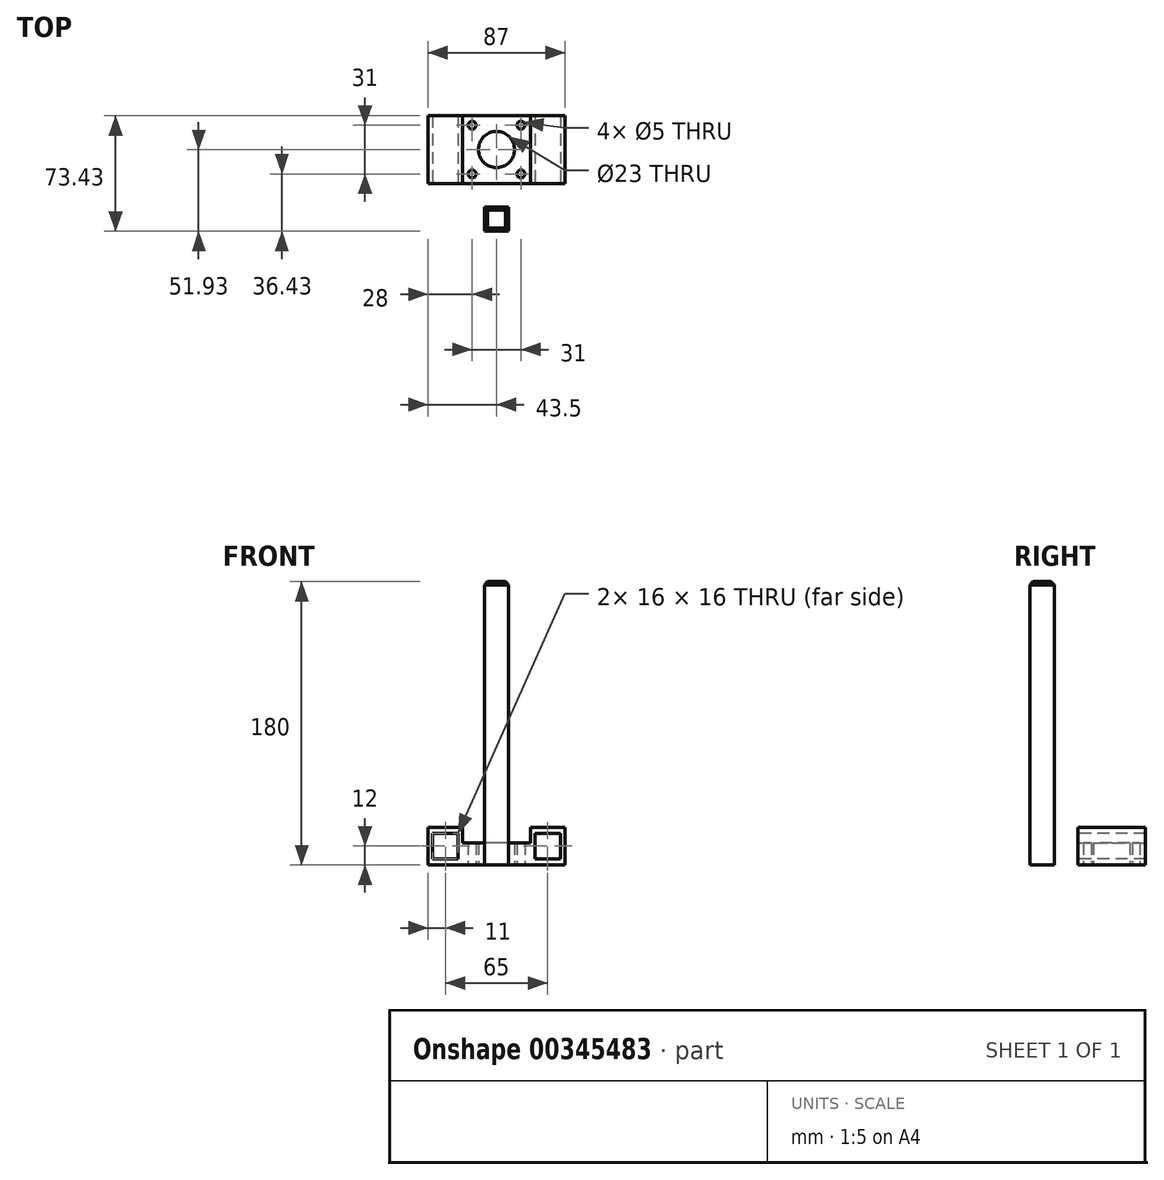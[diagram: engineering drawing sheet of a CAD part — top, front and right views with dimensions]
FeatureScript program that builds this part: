
annotation { "Feature Type Name" : "Feature", "Feature Type Description" : "" }
export const myFeature = defineFeature(function(context is Context, id is Id, definition is map)
    precondition{}
    {
        {
            var Q0;
            Q0=qCreatedBy(makeId("Top.planeOp"),FACE);
            var sketch = newSketch(context, id + "F0", { "sketchPlane" : qUnion([Q0])});
            skPoint(sketch, "E0", {"position": v(0, 0) * mm});
            skLineSegment(sketch, "E1.bottom", {"start": v(15.5, -15.5) * mm, "end": v(-15.5, -15.5) * mm, "construction": true});
            skLineSegment(sketch, "E1.top", {"start": v(15.5, 15.5) * mm, "end": v(-15.5, 15.5) * mm, "construction": true});
            skLineSegment(sketch, "E1.left", {"start": v(15.5, -15.5) * mm, "end": v(15.5, 15.5) * mm, "construction": true});
            skLineSegment(sketch, "E1.right", {"start": v(-15.5, -15.5) * mm, "end": v(-15.5, 15.5) * mm, "construction": true});
            skCircle(sketch, "E2", {"center": v(15.5, 15.5) * mm, "radius": 2.5 * mm});
            skCircle(sketch, "E3", {"center": v(15.5, -15.5) * mm, "radius": 2.5 * mm});
            skCircle(sketch, "E4", {"center": v(-15.5, -15.5) * mm, "radius": 2.5 * mm});
            skCircle(sketch, "E5", {"center": v(-15.5, 15.5) * mm, "radius": 2.5 * mm});
            skCircle(sketch, "E6", {"center": v(0, 0) * mm, "radius": 11.5 * mm});
            skLineSegment(sketch, "E7.bottom", {"start": v(21.5, -21.5) * mm, "end": v(-21.5, -21.5) * mm});
            skLineSegment(sketch, "E7.top", {"start": v(21.5, 21.5) * mm, "end": v(-21.5, 21.5) * mm});
            skLineSegment(sketch, "E7.left", {"start": v(21.5, -21.5) * mm, "end": v(21.5, 21.5) * mm});
            skLineSegment(sketch, "E7.right", {"start": v(-21.5, -21.5) * mm, "end": v(-21.5, 21.5) * mm});
            skLineSegment(sketch, "E8.bottom", {"start": v(-21.5, 21.5) * mm, "end": v(-43.5, 21.5) * mm});
            skLineSegment(sketch, "E8.top", {"start": v(-21.5, -21.5) * mm, "end": v(-43.5, -21.5) * mm});
            skLineSegment(sketch, "E8.left", {"start": v(-21.5, 21.5) * mm, "end": v(-21.5, -21.5) * mm});
            skLineSegment(sketch, "E8.right", {"start": v(-43.5, 21.5) * mm, "end": v(-43.5, -21.5) * mm});
            skLineSegment(sketch, "E9.MirrorCS", {"start": v(21.5, 21.5) * mm, "end": v(43.5, 21.5) * mm});
            skLineSegment(sketch, "E10.MirrorCS", {"start": v(43.5, 21.5) * mm, "end": v(43.5, -21.5) * mm});
            skLineSegment(sketch, "E11.MirrorCS", {"start": v(21.5, -21.5) * mm, "end": v(43.5, -21.5) * mm});
            skLineSegment(sketch, "E12.bottom", {"start": v(7.7, -51.93) * mm, "end": v(-7.7, -51.93) * mm});
            skLineSegment(sketch, "E12.top", {"start": v(7.7, -36.53) * mm, "end": v(-7.7, -36.53) * mm});
            skLineSegment(sketch, "E12.left", {"start": v(7.7, -51.93) * mm, "end": v(7.7, -36.53) * mm});
            skLineSegment(sketch, "E12.right", {"start": v(-7.7, -51.93) * mm, "end": v(-7.7, -36.53) * mm});
            skPoint(sketch, "E12.middle", {"position": v(0, -44.23) * mm});
            skSolve(sketch);
        }
        {
            var Q0;
            Q0=makeQuery(id+"F0.imprint","IMPRINT",FACE,{"disambiguationData":[TD([[makeQuery(id+"F0.imprint","IMPRINT",EDGE,{"derivedFrom":sQuery(id+"F0.wireOp",EDGE,"E2")}),-1.0]])]});
            extrude(context, id + "F1", {"entities" : qUnion([Q0]), "depth" : 14 * mm});
        }
        {
            var Q0;
            Q0=makeQuery(id+"F0.imprint","IMPRINT",FACE,{"disambiguationData":[TD([[makeQuery(id+"F0.imprint","IMPRINT",EDGE,{"derivedFrom":sQuery(id+"F0.wireOp",EDGE,"E8.bottom")}),1.0]])]});
            var Q1;
            Q1=makeQuery(id+"F0.imprint","IMPRINT",FACE,{"disambiguationData":[TD([[makeQuery(id+"F0.imprint","IMPRINT",EDGE,{"derivedFrom":sQuery(id+"F0.wireOp",EDGE,"E7.left")}),-1.0]])]});
            extrude(context, id + "F2", {"entities" : qUnion([Q0, Q1]), "operationType" : NewBodyOperationType.ADD, "depth" : 24 * mm});
        }
        {
            var Q0;
            Q0=makeQuery(id+"F2.opExtrude","SWEPT_FACE",FACE,{"disambiguationData":[OSD([sQuery(id+"F0.wireOp",EDGE,"E8.top")])]});
            var sketch = newSketch(context, id + "F3", { "sketchPlane" : qUnion([Q0])});
            skLineSegment(sketch, "E13.bottom", {"start": v(-24.5, 4) * mm, "end": v(-40.5, 4) * mm});
            skLineSegment(sketch, "E13.top", {"start": v(-24.5, 20) * mm, "end": v(-40.5, 20) * mm});
            skLineSegment(sketch, "E13.left", {"start": v(-24.5, 4) * mm, "end": v(-24.5, 20) * mm});
            skLineSegment(sketch, "E13.right", {"start": v(-40.5, 4) * mm, "end": v(-40.5, 20) * mm});
            skPoint(sketch, "E13.middle", {"position": v(-32.5, 12) * mm});
            skLineSegment(sketch, "E14.MirrorCS", {"start": v(24.5, 4) * mm, "end": v(40.5, 4) * mm});
            skLineSegment(sketch, "E15.MirrorCS", {"start": v(24.5, 4) * mm, "end": v(24.5, 20) * mm});
            skPoint(sketch, "E16.MirrorP", {"position": v(32.5, 12) * mm});
            skLineSegment(sketch, "E17.MirrorCS", {"start": v(40.5, 4) * mm, "end": v(40.5, 20) * mm});
            skLineSegment(sketch, "E18.MirrorCS", {"start": v(24.5, 20) * mm, "end": v(40.5, 20) * mm});
            skSolve(sketch);
        }
        {
            var Q0;
            Q0=makeQuery(id+"F3.imprint","IMPRINT",FACE,{"disambiguationData":[TD([[makeQuery(id+"F3.imprint","IMPRINT",EDGE,{"derivedFrom":sQuery(id+"F3.wireOp",EDGE,"E13.bottom")}),-1.0]])]});
            var Q1;
            Q1=makeQuery(id+"F3.imprint","IMPRINT",FACE,{"disambiguationData":[TD([[makeQuery(id+"F3.imprint","IMPRINT",EDGE,{"derivedFrom":sQuery(id+"F3.wireOp",EDGE,"E14.MirrorCS")}),1.0]])]});
            extrude(context, id + "F4", {"entities" : qUnion([Q0, Q1]), "operationType" : NewBodyOperationType.REMOVE, "endBound" : BoundingType.UP_TO_NEXT, "oppositeDirection" : true, "depth" : 25 * mm});
        }
        {
            var Q0;
            Q0=makeQuery(id+"F0.imprint","IMPRINT",FACE,{"disambiguationData":[TD([[makeQuery(id+"F0.imprint","IMPRINT",EDGE,{"derivedFrom":sQuery(id+"F0.wireOp",EDGE,"E12.bottom")}),-1.0]])]});
            extrude(context, id + "F5", {"entities" : qUnion([Q0]), "depth" : 180 * mm});
        }
        {
            var Q0;
            Q0=makeQuery(id+"F5.opExtrude","CAP_EDGE",EDGE,{"disambiguationData":[OSD([sQuery(id+"F0.wireOp",EDGE,"E12.bottom")])],"isStart":false});
            var Q1;
            Q1=makeQuery(id+"F5.opExtrude","CAP_EDGE",EDGE,{"disambiguationData":[OSD([sQuery(id+"F0.wireOp",EDGE,"E12.left")])],"isStart":false});
            var Q2;
            Q2=makeQuery(id+"F5.opExtrude","CAP_EDGE",EDGE,{"disambiguationData":[OSD([sQuery(id+"F0.wireOp",EDGE,"E12.right")])],"isStart":false});
            var Q3;
            Q3=makeQuery(id+"F5.opExtrude","CAP_EDGE",EDGE,{"disambiguationData":[OSD([sQuery(id+"F0.wireOp",EDGE,"E12.top")])],"isStart":false});
            chamfer(context, id + "F6", {"entities" : qUnion([Q0, Q1, Q2, Q3]), "width" : 2 * mm, "tangentPropagation" : true});
        }
    });
